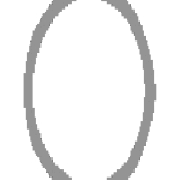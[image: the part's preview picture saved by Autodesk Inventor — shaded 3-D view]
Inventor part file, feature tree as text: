
AUTODESK INVENTOR PART (.ipt)
format: ipt  version: 2021 (Build 250183000, 183)  size: 109,056 bytes
history: native  units: in
note: dims shown in document units (in); Inventor stores cm internally (conversion verified against a paired STEP export)
features: other x4, sketch x3, plane x1
ambient origin geometry x8: Origin, YZ Plane, XZ Plane, XY Plane, X Axis, Y Axis, Z Axis, Center Point
bodies: Solid1 (feature_tree), Body (feature_tree)
feature tree (8):
  other  "Driven Length"
  other  "Frame Generator"
  other  "Start Plane"
  other  "End Plane"
  sketch  "Sketch"  dims[d2=36.7222in d4=-0.0in d5=36.7222in d6=0.12in d7=0.0in d10=90.0deg d9=36.7222in]
  sketch  "Sketch4"  dims[d0=1.0in]
  plane  "Work Plane4"
  sketch  "Sketch5"  dims[d1=0.065in]
